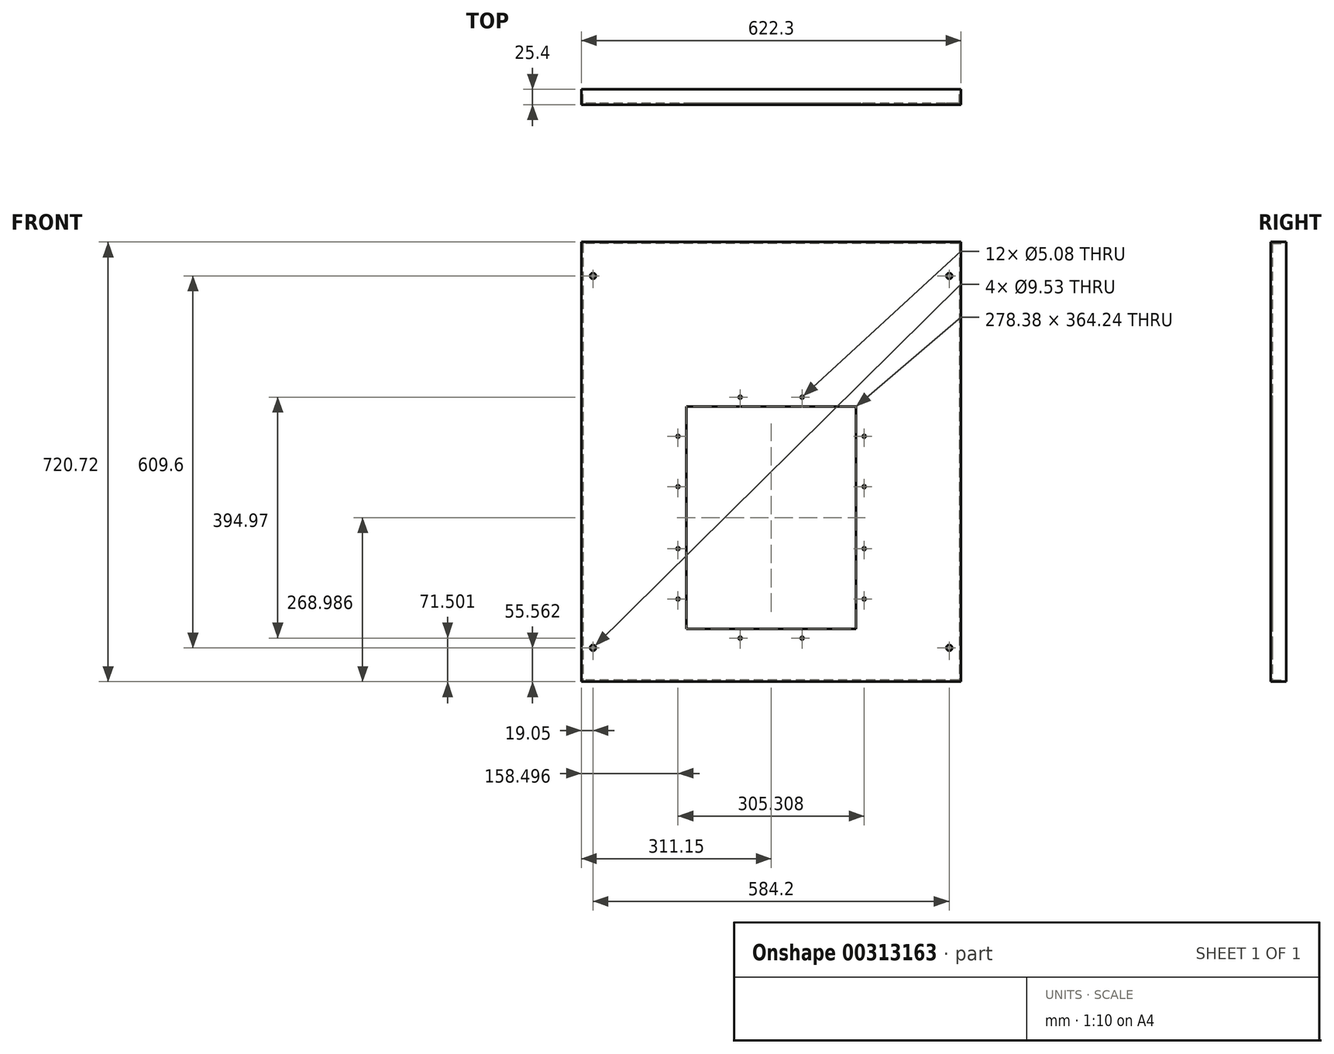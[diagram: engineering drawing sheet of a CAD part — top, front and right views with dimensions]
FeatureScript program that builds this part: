
annotation { "Feature Type Name" : "Feature", "Feature Type Description" : "" }
export const myFeature = defineFeature(function(context is Context, id is Id, definition is map)
    precondition{}
    {
        {
            var Q0;
            Q0=qCreatedBy(makeId("Front.planeOp"),FACE);
            var sketch = newSketch(context, id + "F0", { "sketchPlane" : qUnion([Q0])});
            skLineSegment(sketch, "E0.bottom", {"start": v(311.15, 720.72) * mm, "end": v(-311.15, 720.72) * mm});
            skLineSegment(sketch, "E0.top", {"start": v(311.15, 0) * mm, "end": v(-311.15, 0) * mm});
            skLineSegment(sketch, "E0.left", {"start": v(311.15, 720.72) * mm, "end": v(311.15, 0) * mm});
            skLineSegment(sketch, "E0.right", {"start": v(-311.15, 720.72) * mm, "end": v(-311.15, 0) * mm});
            skLineSegment(sketch, "E1.bottom", {"start": v(-139.2, 86.87) * mm, "end": v(139.2, 86.87) * mm});
            skLineSegment(sketch, "E1.top", {"start": v(-139.2, 451.1) * mm, "end": v(139.2, 451.1) * mm});
            skLineSegment(sketch, "E1.left", {"start": v(-139.2, 86.87) * mm, "end": v(-139.2, 451.1) * mm});
            skLineSegment(sketch, "E1.right", {"start": v(139.2, 86.87) * mm, "end": v(139.2, 451.1) * mm});
            skPoint(sketch, "E2", {"position": v(0, 86.87) * mm});
            skPoint(sketch, "E3", {"position": v(-139.2, 268.99) * mm});
            skCircle(sketch, "E4", {"center": v(152.65, 402.34) * mm, "radius": 2.54 * mm});
            skCircle(sketch, "E5", {"center": v(50.8, 466.47) * mm, "radius": 2.54 * mm});
            skCircle(sketch, "E6", {"center": v(-152.65, 402.34) * mm, "radius": 2.54 * mm});
            skCircle(sketch, "E7", {"center": v(-152.65, 319.79) * mm, "radius": 2.54 * mm});
            skCircle(sketch, "E8", {"center": v(-152.65, 135.64) * mm, "radius": 2.54 * mm});
            skCircle(sketch, "E9", {"center": v(50.8, 71.5) * mm, "radius": 2.54 * mm});
            skCircle(sketch, "E10", {"center": v(152.65, 135.64) * mm, "radius": 2.54 * mm});
            skCircle(sketch, "E11", {"center": v(152.65, 319.79) * mm, "radius": 2.54 * mm});
            skCircle(sketch, "E12", {"center": v(292.1, 665.16) * mm, "radius": 4.76 * mm});
            skCircle(sketch, "E13", {"center": v(-292.1, 665.16) * mm, "radius": 4.76 * mm});
            skCircle(sketch, "E14", {"center": v(-292.1, 55.56) * mm, "radius": 4.76 * mm});
            skCircle(sketch, "E15", {"center": v(292.1, 55.56) * mm, "radius": 4.76 * mm});
            skCircle(sketch, "E16", {"center": v(-50.8, 466.47) * mm, "radius": 2.54 * mm});
            skCircle(sketch, "E17", {"center": v(-152.65, 218.19) * mm, "radius": 2.54 * mm});
            skCircle(sketch, "E18", {"center": v(152.65, 218.19) * mm, "radius": 2.54 * mm});
            skCircle(sketch, "E19", {"center": v(-50.8, 71.5) * mm, "radius": 2.54 * mm});
            skLineSegment(sketch, "E20", {"start": v(50.8, 466.47) * mm, "end": v(-50.8, 466.47) * mm, "construction": true});
            skLineSegment(sketch, "E21", {"start": v(-152.65, 402.34) * mm, "end": v(-152.65, 319.79) * mm, "construction": true});
            skLineSegment(sketch, "E22", {"start": v(-152.65, 135.64) * mm, "end": v(-152.65, 218.19) * mm, "construction": true});
            skLineSegment(sketch, "E23", {"start": v(-152.65, 218.19) * mm, "end": v(-152.65, 319.79) * mm, "construction": true});
            skLineSegment(sketch, "E24", {"start": v(152.65, 319.79) * mm, "end": v(152.65, 402.34) * mm, "construction": true});
            skLineSegment(sketch, "E25", {"start": v(152.65, 319.79) * mm, "end": v(152.65, 218.19) * mm, "construction": true});
            skLineSegment(sketch, "E26", {"start": v(152.65, 135.64) * mm, "end": v(152.65, 218.19) * mm, "construction": true});
            skLineSegment(sketch, "E27", {"start": v(50.8, 71.5) * mm, "end": v(-50.8, 71.5) * mm, "construction": true});
            skPoint(sketch, "E28", {"position": v(0, 466.47) * mm});
            skPoint(sketch, "E29", {"position": v(0, 71.5) * mm});
            skPoint(sketch, "E30", {"position": v(152.65, 268.99) * mm});
            skPoint(sketch, "E31", {"position": v(-152.65, 268.99) * mm});
            skLineSegment(sketch, "E32", {"start": v(-152.65, 268.99) * mm, "end": v(152.65, 268.99) * mm, "construction": true});
            skPoint(sketch, "E33", {"position": v(0, 268.99) * mm});
            skLineSegment(sketch, "E34", {"start": v(0, 466.47) * mm, "end": v(0, 71.5) * mm, "construction": true});
            skSolve(sketch);
        }
        {
            var Q0;
            Q0=qSketchRegion(id+"F0",true);
            extrude(context, id + "F1", {"entities" : qUnion([Q0]), "depth" : 25.4 * mm});
        }
        {
            var Q0;
            Q0=makeQuery(id+"F1.opExtrude","CAP_FACE",FACE,{"disambiguationData":[OSD([sQuery(id+"F0.wireOp",EDGE,"E0.bottom"),sQuery(id+"F0.wireOp",EDGE,"E0.top"),sQuery(id+"F0.wireOp",EDGE,"E0.left"),sQuery(id+"F0.wireOp",EDGE,"E0.right"),sQuery(id+"F0.wireOp",EDGE,"DnOeYdpL-yZhG-pMPP-nWlj-HbxDlVvFq81o.bottom"),sQuery(id+"F0.wireOp",EDGE,"DnOeYdpL-yZhG-pMPP-nWlj-HbxDlVvFq81o.top"),sQuery(id+"F0.wireOp",EDGE,"DnOeYdpL-yZhG-pMPP-nWlj-HbxDlVvFq81o.left"),sQuery(id+"F0.wireOp",EDGE,"DnOeYdpL-yZhG-pMPP-nWlj-HbxDlVvFq81o.right"),sQuery(id+"F0.wireOp",EDGE,"xDgMzqlZ-3YCT-1KnM-qA8u-792qYw5lw1JS"),sQuery(id+"F0.wireOp",EDGE,"Mpdr3xRK-0yTI-dkfT-nTdE-cEWg6RnXpa9N"),sQuery(id+"F0.wireOp",EDGE,"UzSud16w-tGWN-ZEeO-kTY7-zgmRVJxoJOe7"),sQuery(id+"F0.wireOp",EDGE,"QdRWkNVw-568D-XgAy-SO4V-4Q89nbcZrelq"),sQuery(id+"F0.wireOp",EDGE,"8aFPr5qc-bRuC-cZr7-87dc-hIFrfZXMsOHR"),sQuery(id+"F0.wireOp",EDGE,"mJVcAo0T-mOHa-Qb8O-DeX9-rnRp2EFAdPQ3"),sQuery(id+"F0.wireOp",EDGE,"58VjJvAl-gczf-lvPp-maZi-m7BX2DlegteS"),sQuery(id+"F0.wireOp",EDGE,"xgLxJu9m-eS83-UV5U-zqJ0-FrWtQ9vBuum0"),sQuery(id+"F0.wireOp",EDGE,"wqzXiebe-RaGP-8YjT-blUU-62aUiCvM27mv"),sQuery(id+"F0.wireOp",EDGE,"zmVhXP7j-02Ai-JLcr-0Ks7-3LBVpZUHfUrI"),sQuery(id+"F0.wireOp",EDGE,"BW3LuwXz-W35X-CTuh-aFvS-jlk6UlRIqyyT"),sQuery(id+"F0.wireOp",EDGE,"GNJOQj1j-LiCZ-vYCN-EfaB-cui9jyFQZn0N"),sQuery(id+"F0.wireOp",EDGE,"da7037a2-8101-4e2d-bd9b-c90a86b3fb6c.1.0.1"),sQuery(id+"F0.wireOp",EDGE,"da7037a2-8101-4e2d-bd9b-c90a86b3fb6c.1.0.2"),sQuery(id+"F0.wireOp",EDGE,"da7037a2-8101-4e2d-bd9b-c90a86b3fb6c.1.0.3"),sQuery(id+"F0.wireOp",EDGE,"da7037a2-8101-4e2d-bd9b-c90a86b3fb6c.1.0.4"),sQuery(id+"F0.wireOp",EDGE,"da7037a2-8101-4e2d-bd9b-c90a86b3fb6c.1.0.5"),sQuery(id+"F0.wireOp",EDGE,"da7037a2-8101-4e2d-bd9b-c90a86b3fb6c.1.0.6"),sQuery(id+"F0.wireOp",EDGE,"da7037a2-8101-4e2d-bd9b-c90a86b3fb6c.1.0.7"),sQuery(id+"F0.wireOp",EDGE,"da7037a2-8101-4e2d-bd9b-c90a86b3fb6c.1.0.8"),sQuery(id+"F0.wireOp",EDGE,"da7037a2-8101-4e2d-bd9b-c90a86b3fb6c.1.0.9"),sQuery(id+"F0.wireOp",EDGE,"da7037a2-8101-4e2d-bd9b-c90a86b3fb6c.1.0.10"),sQuery(id+"F0.wireOp",EDGE,"da7037a2-8101-4e2d-bd9b-c90a86b3fb6c.1.0.11"),sQuery(id+"F0.wireOp",EDGE,"da7037a2-8101-4e2d-bd9b-c90a86b3fb6c.1.0.12"),sQuery(id+"F0.wireOp",EDGE,"da7037a2-8101-4e2d-bd9b-c90a86b3fb6c.1.0.13"),sQuery(id+"F0.wireOp",EDGE,"da7037a2-8101-4e2d-bd9b-c90a86b3fb6c.1.0.14"),sQuery(id+"F0.wireOp",EDGE,"da7037a2-8101-4e2d-bd9b-c90a86b3fb6c.1.0.15"),sQuery(id+"F0.wireOp",EDGE,"da7037a2-8101-4e2d-bd9b-c90a86b3fb6c.1.0.16")])],"isStart":true});
            shell(context, id + "F2", {"entities" : qUnion([Q0]), "thickness" : 2.54 * mm});
        }
        {
            var Q0;
            Q0=makeQuery(id+"F2.opShell","OFFSET_FACE",FACE,{"disambiguationData":[OSD([sQuery(id+"F0.wireOp",EDGE,"E0.bottom")])]});
            var sketch = newSketch(context, id + "F3", { "sketchPlane" : qUnion([Q0])});
            skLineSegment(sketch, "E35.bottom", {"start": v(308.61, 0) * mm, "end": v(-308.6, 0) * mm});
            skLineSegment(sketch, "E35.top", {"start": v(308.61, 22.86) * mm, "end": v(-308.6, 22.86) * mm});
            skLineSegment(sketch, "E35.left", {"start": v(308.61, 0) * mm, "end": v(308.61, 22.86) * mm});
            skLineSegment(sketch, "E35.right", {"start": v(-308.6, 0) * mm, "end": v(-308.6, 22.86) * mm});
            skSolve(sketch);
        }
        {
            var Q0;
            Q0 = qSketchRegion(id + "F3", true);
            var Q1;
            Q1=makeQuery(id+"F2.opShell","OFFSET_FACE",FACE,{"disambiguationData":[OSD([sQuery(id+"F0.wireOp",EDGE,"E0.top")])]});
            extrude(context, id + "F4", {"entities" : qUnion([Q0]), "operationType" : NewBodyOperationType.REMOVE, "endBound" : BoundingType.UP_TO_SURFACE, "endBoundEntityFace" : qUnion([Q1]), "depth" : 25.4 * mm});
        }
    });
